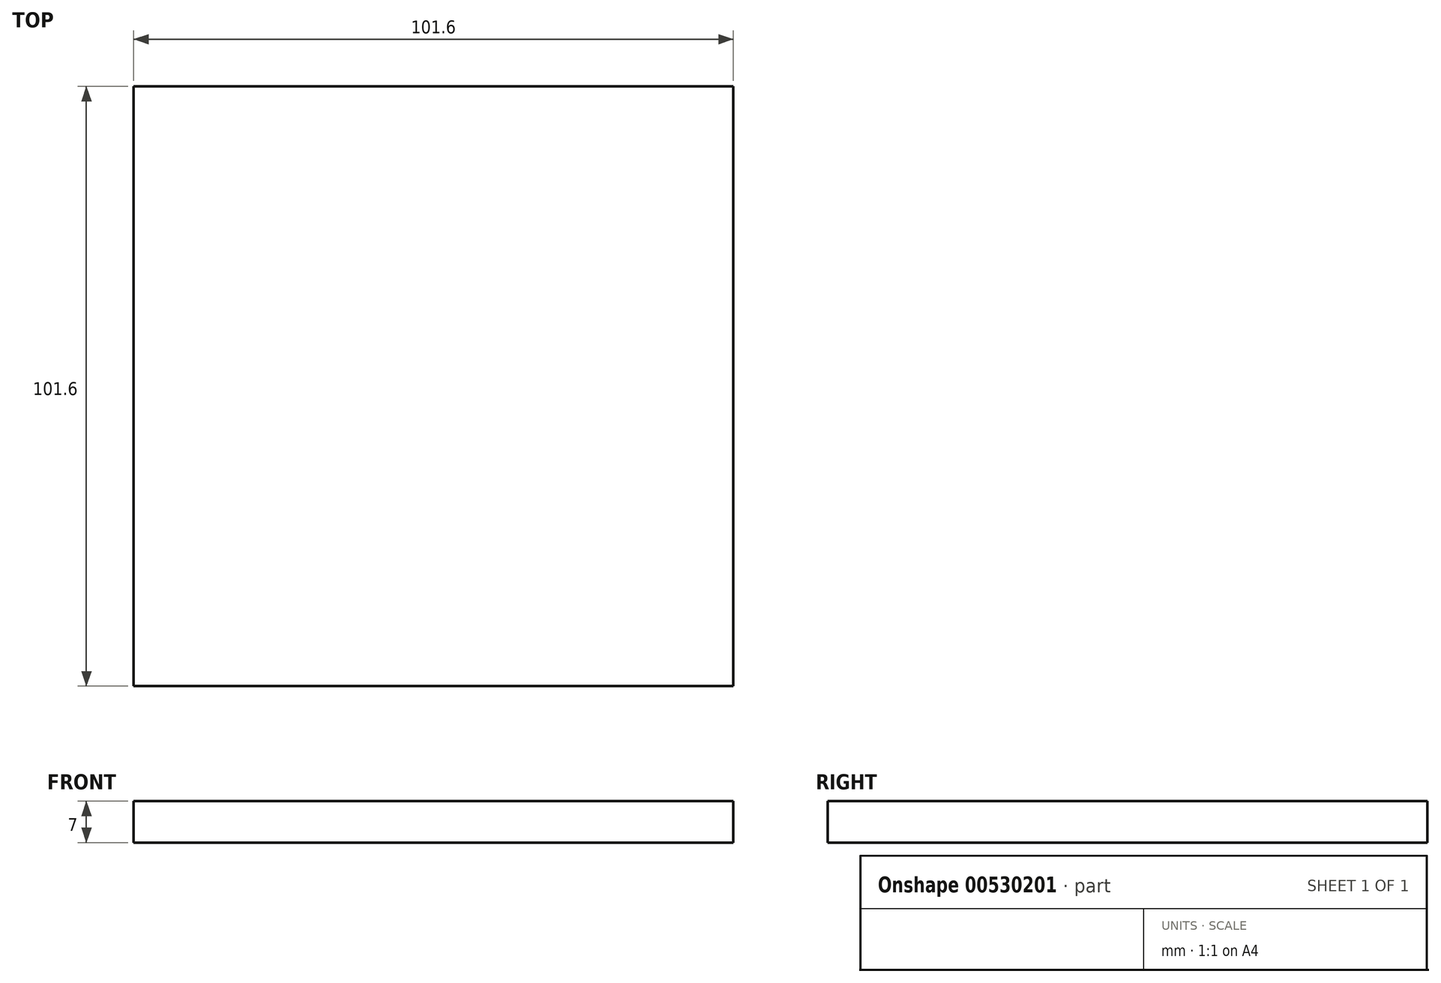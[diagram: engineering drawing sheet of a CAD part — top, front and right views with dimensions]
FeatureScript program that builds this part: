
annotation { "Feature Type Name" : "Feature", "Feature Type Description" : "" }
export const myFeature = defineFeature(function(context is Context, id is Id, definition is map)
    precondition{}
    {
        {
            var Q0;
            Q0=qCreatedBy(makeId("Top.planeOp"),FACE);
            var sketch = newSketch(context, id + "F0", { "sketchPlane" : qUnion([Q0])});
            skLineSegment(sketch, "E0.bottom", {"start": v(50.8, 50.8) * mm, "end": v(-50.8, 50.8) * mm});
            skLineSegment(sketch, "E0.top", {"start": v(50.8, -50.8) * mm, "end": v(-50.8, -50.8) * mm});
            skLineSegment(sketch, "E0.left", {"start": v(50.8, 50.8) * mm, "end": v(50.8, -50.8) * mm});
            skLineSegment(sketch, "E0.right", {"start": v(-50.8, 50.8) * mm, "end": v(-50.8, -50.8) * mm});
            skPoint(sketch, "E0.middle", {"position": v(0, 0) * mm});
            skSolve(sketch);
        }
        {
            var Q0;
            Q0=makeQuery(id+"F0.imprint","IMPRINT",FACE,{"disambiguationData":[TD([[makeQuery(id+"F0.imprint","IMPRINT",EDGE,{"derivedFrom":sQuery(id+"F0.wireOp",EDGE,"E0.bottom")}),1.0]])]});
            extrude(context, id + "F1", {"entities" : qUnion([Q0]), "depth" : 7 * mm, "offsetDistance" : 25.4 * mm});
        }
    });
